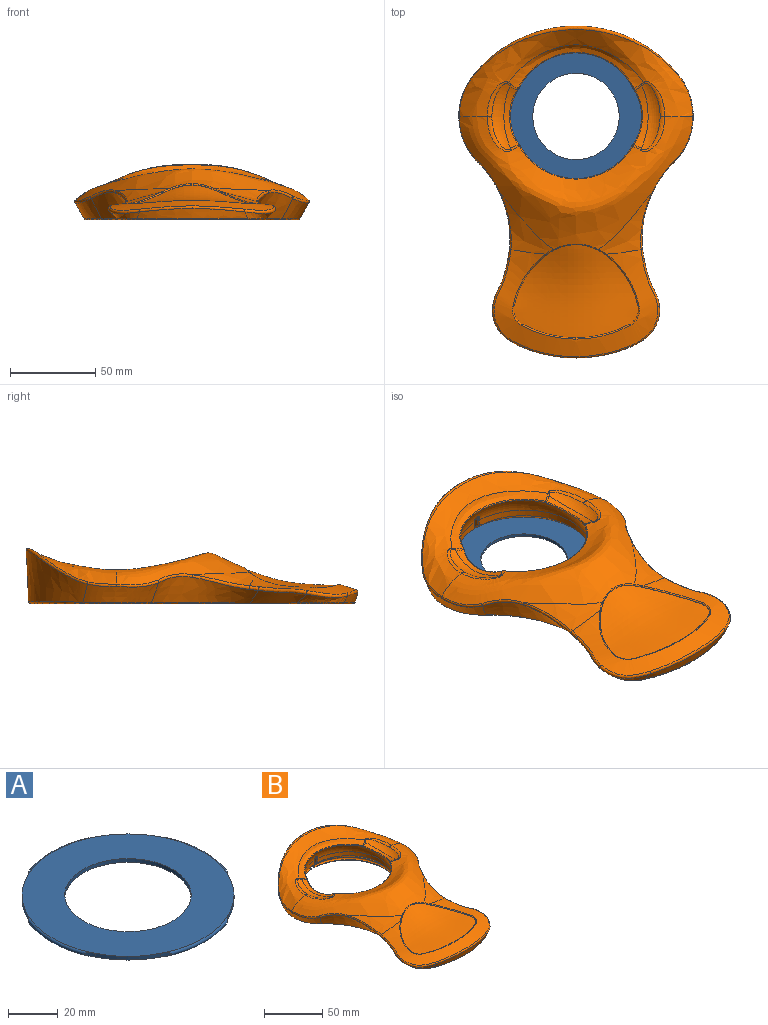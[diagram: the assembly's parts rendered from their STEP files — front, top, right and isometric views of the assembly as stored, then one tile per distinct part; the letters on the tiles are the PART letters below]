
ASSEMBLY  parts=2 mates=1
PART A: 19 faces, bbox 94.1x94.1x1.8 mm
  f0: cylinder r=42.56mm len=18.64mm, axis (0,0,-1), area 49mm2, adj f8,f9,f16,f17
  f1: cylinder r=42.56mm len=18.64mm, axis (0,0,-1), area 49mm2, adj f10,f11,f16,f17
  f2: cylinder r=42.56mm len=18.64mm, axis (0,0,-1), area 49mm2, adj f4,f5,f16,f17
  f3: cylinder r=25.4mm len=50.8mm, axis (0,0,-1), area 291.9mm2, adj f16,f17
  f4: cylinder r=12.7mm len=3.41mm, axis (0,0,-1), area 5.4mm2, adj f2,f15
  f5: cylinder r=12.7mm len=3.41mm, axis (0,0,-1), area 5.4mm2, adj f2,f18
  f6: cylinder r=12.7mm len=3.41mm, axis (0,0,-1), area 5.4mm2, adj f12,f18
  f7: cylinder r=12.7mm len=3.41mm, axis (0,0,-1), area 5.4mm2, adj f12,f14
  f8: cylinder r=12.7mm len=3.41mm, axis (0,0,-1), area 5.4mm2, adj f0,f14
  f9: cylinder r=12.7mm len=3.41mm, axis (0,0,-1), area 5.4mm2, adj f0,f13
  f10: cylinder r=12.7mm len=3.41mm, axis (0,0,-1), area 5.4mm2, adj f1,f15
  f11: cylinder r=12.7mm len=3.41mm, axis (0,0,-1), area 5.4mm2, adj f1,f13
  f12: cylinder r=42.56mm len=18.64mm, axis (0,0,-1), area 49mm2, adj f6,f7,f16,f17
  f13: torus R=42.56mm, axis (0,0,-1), area 104.6mm2, adj f9,f11,f16,f17
  f14: torus R=42.56mm, axis (0,0,-1), area 104.6mm2, adj f7,f8,f16,f17
  f15: torus R=42.56mm, axis (0,0,-1), area 104.6mm2, adj f4,f10,f16,f17
  f16: plane 85.11x85.11mm, normal (0,0,-1), area 3662.6mm2, adj f0,f1,f2,f3,f12,f13,f14,f15
  f17: plane 85.11x85.11mm, normal (0,0,1), area 3662.6mm2, adj f0,f1,f2,f3,f12,f13,f14,f15
  f18: torus R=42.56mm, axis (0,0,-1), area 104.6mm2, adj f5,f6,f16,f17
PART B: 147 faces, bbox 160.8x204.3x46.3 mm
  f0: bspline ~30.8x19.86mm, area 39.9mm2, adj f1,f4,f18,f45
  f1: bspline ~11.04x5.88mm, area 13.4mm2, adj f0,f2,f17,f45
  f2: bspline ~32.09x8.86mm, area 36.1mm2, adj f1,f3,f16,f45
  f3: bspline ~32.09x8.86mm, area 36.1mm2, adj f2,f15,f39,f45
  f4: bspline ~0.96x0.84mm, area 0.5mm2, adj f0,f5,f18,f133
  f5: bspline ~0.77x0.76mm, area 0.3mm2, adj f4,f13,f19,f133
  f6: bspline ~30.8x19.86mm, area 39.9mm2, adj f7,f15,f38,f45
  f7: bspline ~0.96x0.84mm, area 0.5mm2, adj f6,f9,f22,f38
  f8: bspline ~4.56x2.83mm, area 5.1mm2, adj f9,f10,f22,f42
  f9: bspline ~0.77x0.76mm, area 0.3mm2, adj f7,f8,f22,f41
  f10: bspline ~0.82x0.78mm, area 0.4mm2, adj f8,f12,f23,f42
  f11: bspline ~12.83x3.36mm, area 12.8mm2, adj f12,f14,f21,f23
  f12: bspline ~12.83x3.36mm, area 12.8mm2, adj f10,f11,f23,f43
  f13: bspline ~4.56x2.81mm, area 5.1mm2, adj f5,f14,f20,f133
  f14: bspline ~0.82x0.78mm, area 0.4mm2, adj f11,f13,f20,f23
  f15: bspline ~11.04x6mm, area 13.4mm2, adj f3,f6,f40,f45
  f16: bspline ~31.68x8.11mm, area 1.3mm2, adj f2,f17,f39,f44
  f17: bspline ~10.27x4.98mm, area 0.6mm2, adj f1,f16,f18,f44
  f18: bspline ~30.77x19.57mm, area 2.3mm2, adj f0,f4,f17,f19,f44
  f19: plane 0.23x0.19mm, normal (-0.62,-0.78,-0.11), area 0mm2, adj f5,f18,f20,f44
  f20: bspline ~4.36x2.65mm, area 0.6mm2, adj f13,f14,f19,f21,f44
  f21: bspline ~12.39x2.92mm, area 2.1mm2, adj f11,f20,f43,f44
  f22: bspline ~52.07x36.55mm, area 401.5mm2, adj f7,f8,f9,f23,f45,f124
  f23: bspline ~154.44x80.39mm, area 5140.2mm2, adj f10,f11,f12,f14,f22,f30,f32,f117
  f24: bspline ~1.2x1.08mm, area 1.2mm2, adj f30,f31,f32,f37
  f25: bspline ~1.32x1.09mm, area 1.3mm2, adj f26,f27,f36,f37
  f26: bspline ~32.07x6.21mm, area 32.5mm2, adj f25,f28,f37,f100
  f27: bspline ~67.88x21.15mm, area 76.5mm2, adj f25,f29,f35,f37
  f28: bspline ~1.2x1.08mm, area 1.2mm2, adj f26,f30,f37,f144
  f29: bspline ~1.32x1.09mm, area 1.3mm2, adj f27,f31,f34,f37
  f30: bspline ~66.62x21.4mm, area 73.5mm2, adj f23,f24,f28,f37
  f31: bspline ~32.06x5.89mm, area 32.5mm2, adj f24,f29,f33,f37
  f32: bspline ~5.07x3.38mm, area 6mm2, adj f23,f24,f33,f138
  f33: cone r=29.89mm half-angle=45deg, axis (-0.71,0,0.71), area 179.1mm2, adj f31,f32,f34,f140
  f34: bspline ~4.88x3.27mm, area 6mm2, adj f29,f33,f35,f137
  f35: bspline ~82.62x25.48mm, area 533.2mm2, adj f27,f34,f36,f137,f139,f141,f142,f145
  f36: bspline ~4.88x3.28mm, area 6mm2, adj f25,f35,f100,f141
  f37: revolved ~78.46x78.46mm, area 2011.1mm2, adj f24,f25,f26,f27,f28,f29,f30,f31
  f38: bspline ~30.77x19.57mm, area 2.3mm2, adj f6,f7,f40,f41,f44
  f39: bspline ~31.68x8.11mm, area 1.3mm2, adj f3,f16,f40,f44
  f40: bspline ~10.27x5.14mm, area 0.6mm2, adj f15,f38,f39,f44
  f41: plane 0.23x0.18mm, normal (0.62,-0.78,-0.11), area 0mm2, adj f9,f38,f42,f44
  f42: bspline ~4.36x2.65mm, area 0.6mm2, adj f8,f10,f41,f43,f44
  f43: bspline ~12.39x2.92mm, area 2.1mm2, adj f12,f21,f42,f44
  f44: bspline ~73.87x56.03mm, area 3065.9mm2, adj f16,f17,f18,f19,f20,f21,f38,f39
  f45: bspline ~115.78x73.43mm, area 2047mm2, adj f0,f1,f2,f3,f6,f15,f22,f125
  f46: bspline ~4.32x4.32mm, area 5.9mm2, adj f47,f48,f57,f58,f59,f78
  f47: cylinder r=0.76mm len=0.98mm, axis (0,0,1), area 0.6mm2, adj f46,f53,f57,f78
  f48: cylinder r=0.76mm len=4.07mm, axis (0,0,1), area 4.5mm2, adj f46,f49,f58,f78
  f49: bspline ~0.78x0.72mm, area 0.6mm2, adj f37,f48,f50,f78
  f50: bspline ~4.61x3.12mm, area 6.1mm2, adj f37,f49,f51,f79
  f51: bspline ~0.78x0.72mm, area 0.6mm2, adj f37,f50,f52,f81
  f52: cylinder r=0.76mm len=4.07mm, axis (0,0,-1), area 4.5mm2, adj f51,f54,f58,f81
  f53: bspline ~3.99x1.78mm, area 4.2mm2, adj f47,f57,f66,f74,f75,f76,f77,f78
  f54: bspline ~4.32x4.32mm, area 5.9mm2, adj f52,f55,f58,f59,f60,f81
  f55: cylinder r=0.76mm len=0.98mm, axis (0,0,-1), area 0.6mm2, adj f54,f56,f60,f81
  f56: bspline ~3.99x1.78mm, area 4.2mm2, adj f55,f60,f61,f62,f63,f64,f68,f81
  f57: cylinder r=42.81mm len=84.65mm, axis (0,0,-1), area 81.4mm2, adj f46,f47,f53,f59,f77,f89
  f58: cylinder r=39.25mm len=78.51mm, axis (0,0,-1), area 984.3mm2, adj f37,f46,f48,f52,f54,f59
  f59: cone r=40.9mm half-angle=45deg, axis (0,0,-1), area 1218.5mm2, adj f46,f54,f57,f58,f60,f86,f87,f89
  f60: cylinder r=42.81mm len=84.65mm, axis (0,0,-1), area 81.4mm2, adj f54,f55,f56,f59,f61,f87
  f61: torus R=42.56mm, axis (0,0,1), area 433.4mm2, adj f56,f60,f62,f87,f88,f97
  f62: cylinder r=42.81mm len=84.5mm, axis (0,0,-1), area 34.3mm2, adj f56,f61,f63,f67,f85,f97
  f63: cylinder r=0.76mm len=0.5mm, axis (0,0,-1), area 0.1mm2, adj f56,f62,f64
  f64: bspline ~0.67x0.6mm, area 0.4mm2, adj f56,f63,f67,f68
  f65: bspline ~0.38x0.38mm, area 0mm2, adj f66,f74,f76,f84
  f66: bspline ~0.67x0.6mm, area 0.4mm2, adj f53,f65,f74,f75
  f67: bspline ~0.38x0.38mm, area 0mm2, adj f62,f64,f68,f85
  f68: cylinder r=0.76mm len=7.33mm, axis (0,1,0), area 8.5mm2, adj f56,f64,f67,f69,f81,f99
  f69: bspline ~1.28x1.26mm, area 1.9mm2, adj f68,f70,f81,f102
  f70: bspline ~2.1x0.8mm, area 2.6mm2, adj f69,f71,f81,f82
  f71: bspline ~4.75x2.89mm, area 9.8mm2, adj f70,f72,f80,f82
  f72: bspline ~2.09x0.81mm, area 2.5mm2, adj f71,f73,f78,f82
  f73: bspline ~1.28x1.26mm, area 1.9mm2, adj f72,f74,f78,f83
  f74: cylinder r=0.76mm len=7.34mm, axis (0,-1,0), area 8.5mm2, adj f53,f65,f66,f73,f78,f99
  f75: cylinder r=0.76mm len=0.5mm, axis (0,0,1), area 0.1mm2, adj f53,f66,f76
  f76: cylinder r=42.81mm len=84.5mm, axis (0,0,-1), area 34.3mm2, adj f53,f65,f75,f77,f84,f91
  f77: torus R=42.56mm, axis (0,0,1), area 433.5mm2, adj f53,f57,f76,f89,f90,f91
  f78: plane 17.58x17.43mm, normal (1,0,0), area 55.7mm2, adj f46,f47,f48,f49,f53,f72,f73,f74
  f79: cylinder r=1.59mm len=9.23mm, axis (0,0.79,-0.62), area 6.6mm2, adj f50,f78,f81
  f80: cylinder r=1.59mm len=6.52mm, axis (0,0.79,-0.62), area 17.5mm2, adj f71,f78,f81
  f81: plane 17.58x17.42mm, normal (-1,0,0), area 55.7mm2, adj f51,f52,f54,f55,f56,f68,f69,f70
  f82: bspline ~130.13x36.67mm, area 3427.2mm2, adj f70,f71,f72,f83,f102,f115,f120,f132
  f83: bspline ~56.2x32.59mm, area 125mm2, adj f73,f82,f99,f103
  f84: torus R=43.19mm, axis (0,0,1), area 73.6mm2, adj f65,f76,f95,f99
  f85: torus R=43.19mm, axis (0,0,1), area 73.6mm2, adj f62,f67,f93,f99
  f86: bspline ~17.47x3.48mm, area 16mm2, adj f59,f87,f89,f98
  f87: bspline ~1.03x0.84mm, area 0.6mm2, adj f59,f60,f61,f86,f88,f98
  f88: bspline ~3.3x1.66mm, area 3.2mm2, adj f61,f87,f94,f96,f97,f98
  f89: bspline ~1.03x0.84mm, area 0.6mm2, adj f57,f59,f77,f86,f90,f98
  f90: bspline ~3.3x1.73mm, area 3.2mm2, adj f77,f89,f91,f92,f96,f98
  f91: bspline ~0.58x0.42mm, area 0.1mm2, adj f76,f77,f90,f92,f95
  f92: bspline ~0.67x0.46mm, area 0.3mm2, adj f90,f91,f95,f96
  f93: bspline ~0.39x0.38mm, area 0.1mm2, adj f85,f94,f97,f99
  f94: bspline ~0.67x0.46mm, area 0.3mm2, adj f88,f93,f96,f97
  f95: bspline ~0.39x0.38mm, area 0.1mm2, adj f84,f91,f92,f99
  f96: torus R=11.61mm, axis (0,0,1), area 38.2mm2, adj f88,f90,f92,f94,f98,f99
  f97: bspline ~0.58x0.42mm, area 0.1mm2, adj f61,f62,f88,f93,f94
  f98: sphere r=11.11mm, area 618.6mm2, adj f86,f87,f88,f89,f90,f96
  f99: plane 189.62x124.76mm, normal (0,0,-1), area 9339.4mm2, adj f68,f74,f83,f84,f85,f93,f95,f96
  f100: cone r=29.89mm half-angle=45deg, axis (0.71,0,0.71), area 179.2mm2, adj f26,f36,f144,f146
  f101: bspline ~40.38x10.95mm, area 57.9mm2, adj f99,f102,f110,f115
  f102: bspline ~56.23x32.62mm, area 123.1mm2, adj f69,f82,f99,f101
  f103: bspline ~40.41x10.95mm, area 58mm2, adj f83,f99,f104,f132
  f104: bspline ~58.71x24.72mm, area 80.2mm2, adj f99,f103,f105,f136
  f105: bspline ~28.38x11.92mm, area 26.9mm2, adj f99,f104,f106,f135
  f106: bspline ~27.5x12.27mm, area 41.5mm2, adj f99,f105,f107,f134
  f107: bspline ~65.24x7.79mm, area 107.9mm2, adj f99,f106,f108,f111
  f108: bspline ~27.54x12.07mm, area 42mm2, adj f99,f107,f109,f112
  f109: bspline ~28.3x11.87mm, area 26.9mm2, adj f99,f108,f110,f113
  f110: bspline ~58.69x24.69mm, area 80.2mm2, adj f99,f101,f109,f114
  f111: bspline ~65.37x8.34mm, area 332.1mm2, adj f107,f112,f128,f134
  f112: bspline ~29.69x17.66mm, area 154.4mm2, adj f108,f111,f113,f129
  f113: bspline ~33.28x19.57mm, area 311.4mm2, adj f109,f112,f114,f130
  f114: bspline ~63.6x29.92mm, area 971.3mm2, adj f110,f113,f115,f116,f117,f131
  f115: bspline ~44.91x15.68mm, area 504.9mm2, adj f82,f101,f114,f118,f119
  f116: bspline ~33.6x8.67mm, area 77mm2, adj f114,f117,f131,f133
  f117: bspline ~20.29x14.84mm, area 42.6mm2, adj f23,f114,f116,f118
  f118: bspline ~25.07x9.89mm, area 46.5mm2, adj f23,f115,f117,f119
  f119: bspline ~16.63x4.04mm, area 26.7mm2, adj f115,f118,f120,f145
  f120: bspline ~130.19x36.87mm, area 348.2mm2, adj f82,f119,f121,f145
  f121: bspline ~17.12x4.27mm, area 27.5mm2, adj f120,f122,f132,f145
  f122: bspline ~24.89x9.73mm, area 46.1mm2, adj f23,f121,f123,f132
  f123: bspline ~20.47x15mm, area 43mm2, adj f23,f122,f124,f136
  f124: bspline ~33.6x8.67mm, area 77mm2, adj f22,f123,f125,f136
  f125: bspline ~5.92x2.78mm, area 15.5mm2, adj f45,f124,f126,f136
  f126: bspline ~28.61x9.97mm, area 87.4mm2, adj f45,f125,f127,f135
  f127: bspline ~24.26x18.69mm, area 80.2mm2, adj f45,f126,f128,f134
  f128: bspline ~61.77x6.83mm, area 117.5mm2, adj f45,f111,f127,f129
  f129: bspline ~24.41x18.23mm, area 80.3mm2, adj f45,f112,f128,f130
  f130: bspline ~28.43x9.99mm, area 86.9mm2, adj f45,f113,f129,f131
  f131: bspline ~5.76x2.76mm, area 15.1mm2, adj f45,f114,f116,f130
  f132: bspline ~44.76x15.67mm, area 506.8mm2, adj f82,f103,f121,f122,f136
  f133: bspline ~52.07x36.55mm, area 401.5mm2, adj f4,f5,f13,f23,f45,f116
  f134: bspline ~29.85x18.22mm, area 154.4mm2, adj f106,f111,f127,f135
  f135: bspline ~33.61x19.56mm, area 312mm2, adj f105,f126,f134,f136
  f136: bspline ~63.79x30.08mm, area 974.1mm2, adj f104,f123,f124,f125,f132,f135
  f137: bspline ~2.41x2.08mm, area 2.3mm2, adj f34,f35,f139,f140
  f138: bspline ~20.63x14.5mm, area 59.4mm2, adj f23,f32,f139,f140
  f139: bspline ~20.42x12.53mm, area 57.4mm2, adj f35,f137,f138,f140,f145
  f140: torus R=25.4mm, axis (0.71,0,-0.71), area 260.1mm2, adj f33,f137,f138,f139
  f141: bspline ~2.4x2.07mm, area 2.3mm2, adj f35,f36,f142,f146
  f142: bspline ~20.42x12.54mm, area 57.4mm2, adj f35,f141,f143,f145,f146
  f143: bspline ~20.63x14.5mm, area 59.4mm2, adj f23,f142,f144,f146
  f144: bspline ~5.07x3.38mm, area 6mm2, adj f23,f28,f100,f143
  f145: bspline ~144.38x54.13mm, area 2676.7mm2, adj f23,f35,f119,f120,f121,f139,f142
  f146: torus R=25.4mm, axis (-0.71,0,-0.71), area 260.1mm2, adj f100,f141,f142,f143
PLACE A t=(0.27,44.47,-14.31)mm
PLACE B t=(0.27,44.47,-15.55)mm
MATE revolute A.f0 <-> B.f59  axis (0,0,-1) through (0.27,44.47,-12.4)mm
